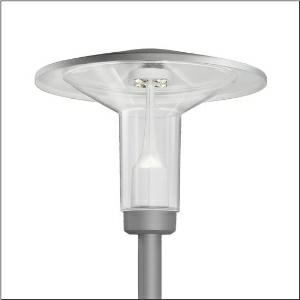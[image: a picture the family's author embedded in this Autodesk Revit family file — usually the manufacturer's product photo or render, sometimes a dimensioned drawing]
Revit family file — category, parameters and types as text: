
# Revit family: laterne_iq___p1_0a_5xa5255bf14hp_c829
name_source: partatom
category: Lighting Fixtures
units: mm (PartAtom-declared; Revit-internal decimal feet)

## family parameters
Cut with Voids When Loaded = No
Host = Face
Light Source = No
Part Type = Normal
Room Calculation Point = No
Round Connector Dimension = Use Diameter
Shared = No

## types (1)
- --- (1 x LED, 3890 lm, 33.6 W, 2200K)
    Apparent Load = 34 VA
    CIE Flux Codes = 34 64 92 97 100
    Color Rendering = 70
    Color Temperature = 2200K
    Default Elevation = 1800 mm
    Description = Lantern iQ, mast luminaire, Module 540 iQ-SR, primary light control with 3 zone facetted reflector, of plastic, silver coated, highly specular, structured, primary optical cover: cover, of PMMA, transparent, light distribution: P1.0a, light emission: direct distribution, primary light characteristic: strongly asymmetric, installation type: post-top, LED, High Power LED, rated luminous flux: 3.890lm, luminous efficacy: 116lm/W, light colour: 722, colour temperature: 2200K, control gear: iQ Street-Remote, control: pre-setting: logarithmic dimming characteristic, Street-Remote, Auto-Match, Temp-Guard, Lumen-Switch, Night-Set, Smart-Wire, Light-Fading, Desk-Remote (wireless, voltage-free reading and setting of iQ features in the workshop via application-optimized NFC function/RFID function), optimised constant luminous flux control (CLO 2.0), with terminal, 6-pole, max. 2.5mm², mains connection: 230..240V, AC, 50/60Hz, start of lifetime: 34W, end of service life: 36W, reduction: 15W, luminaire housing, upper part, of glass-fibre reinforced polyester, coated, Siteco® metallic grey (DB 702S), diameter: 750mm, height: 583mm, spigot size: d x l = 76 x 70mm (post-top) | with reducer (optional accessory) 60 x 70mm, mounting height: 3..5m, post-top mast mounting element, of diecast aluminium, coated, Siteco® metallic grey (DB 702S), Module 540 iQ-SR, traffic white (RAL 9016), equipment: Power, protection rating (complete): IP65, insulation class (complete): insulation class II (safety insulation), certification: CE, ENEC, VDE, packaging unit: 1 piece

Light Distribution: P1.0a
    Height = 583 mm
    Lamp = 1 x LED
    Lamp Light Flux = 3890 lm
    Lamp Power = 33.6 W
    Lamp count = 1
    Length = 750 mm
    Luminous efficacy = 116 lm/W
    Manufacturer = Siteco
    ModVariant = No
    Model = 5XA5255BF14HP
    Number of Poles = 1
    OnlyDefault = Yes
    Power Factor = 1
    Product Name = Laterne iQ | P1.0a
    Product group = mast luminaire | pylon top
    ProductGroupID = 6100
    Protection Class = Protection class II
    Protection Degree = IP 65
    RLX_Detail_Level = 1
    RLX_Emergency_Light_Flux = 0 lm
    RLX_Emergency_Type = 0
    RLX_Emergency_Type_DB = No
    RlxData = <blob elided: 34509 chars, md5=8cf04525>
    Socket = socket
    Standby Power = 0 W
    System Light Flux = 3890 lm
    System Power = 34 W
    Type Comments = factory setting: luminous flux: 100 % | dim-lin: 254 | 695 mA
    Type Image = l_1006050.jpg
    URL = http://relux.com
    VarID = @adj_214731
    Voltage = 0 V
    Weight = 0.00 kg
    Width = 0 mm  [stored 0 ft]

note: [stored X ft] marks values corroborated as IEEE doubles in the binary element streams (Revit-internal decimal feet)

## geometry (parser evidence)
native form markers: Blend x4, Sweep x8
no freeform markers — native parametric forms only
